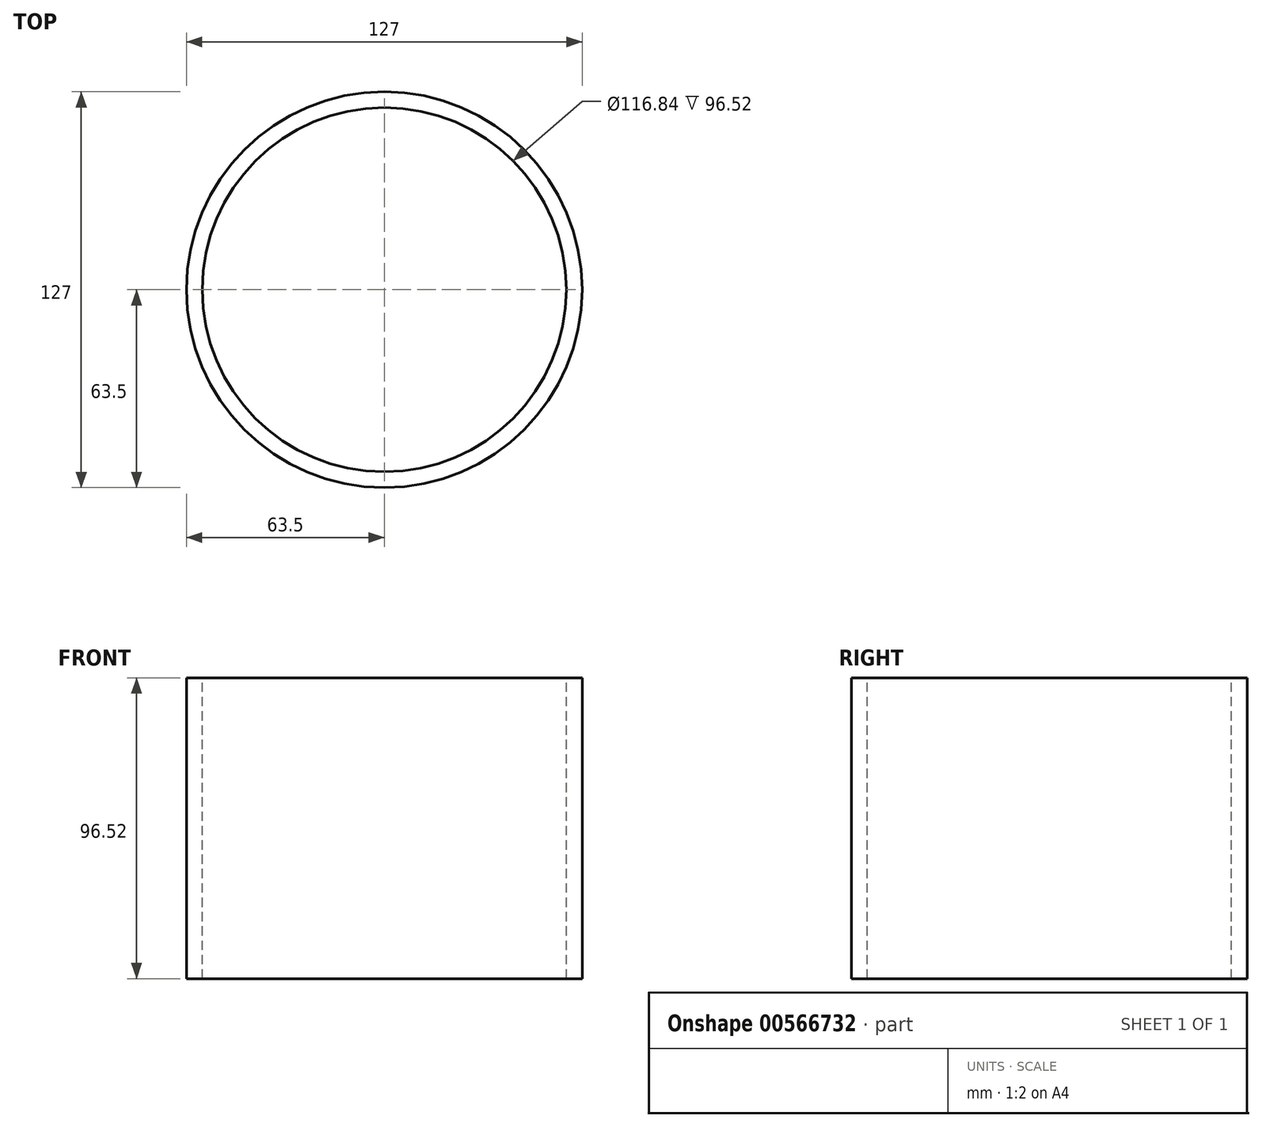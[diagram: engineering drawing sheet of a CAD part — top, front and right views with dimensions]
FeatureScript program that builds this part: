
annotation { "Feature Type Name" : "Feature", "Feature Type Description" : "" }
export const myFeature = defineFeature(function(context is Context, id is Id, definition is map)
    precondition{}
    {
        {
            var Q0;
            Q0=qCreatedBy(makeId("Top.planeOp"),FACE);
            var sketch = newSketch(context, id + "F0", { "sketchPlane" : qUnion([Q0])});
            skCircle(sketch, "E0", {"center": v(0, 0) * mm, "radius": 63.5 * mm});
            skSolve(sketch);
        }
        {
            var Q0;
            Q0=qSketchRegion(id+"F0",true);
            extrude(context, id + "F1", {"entities" : qUnion([Q0]), "endBound" : BoundingType.SYMMETRIC, "depth" : 96.52 * mm, "offsetDistance" : 25.4 * mm});
        }
        {
            var Q0;
            Q0=qCreatedBy(makeId("Top.planeOp"),FACE);
            var sketch = newSketch(context, id + "F2", { "sketchPlane" : qUnion([Q0])});
            skCircle(sketch, "E1", {"center": v(0, 0) * mm, "radius": 58.42 * mm});
            skSolve(sketch);
        }
        {
            var Q0;
            Q0=qSketchRegion(id+"F2",true);
            extrude(context, id + "F3", {"entities" : qUnion([Q0]), "operationType" : NewBodyOperationType.REMOVE, "endBound" : BoundingType.SYMMETRIC, "oppositeDirection" : true, "depth" : 101.6 * mm, "offsetDistance" : 25.4 * mm});
        }
    });
